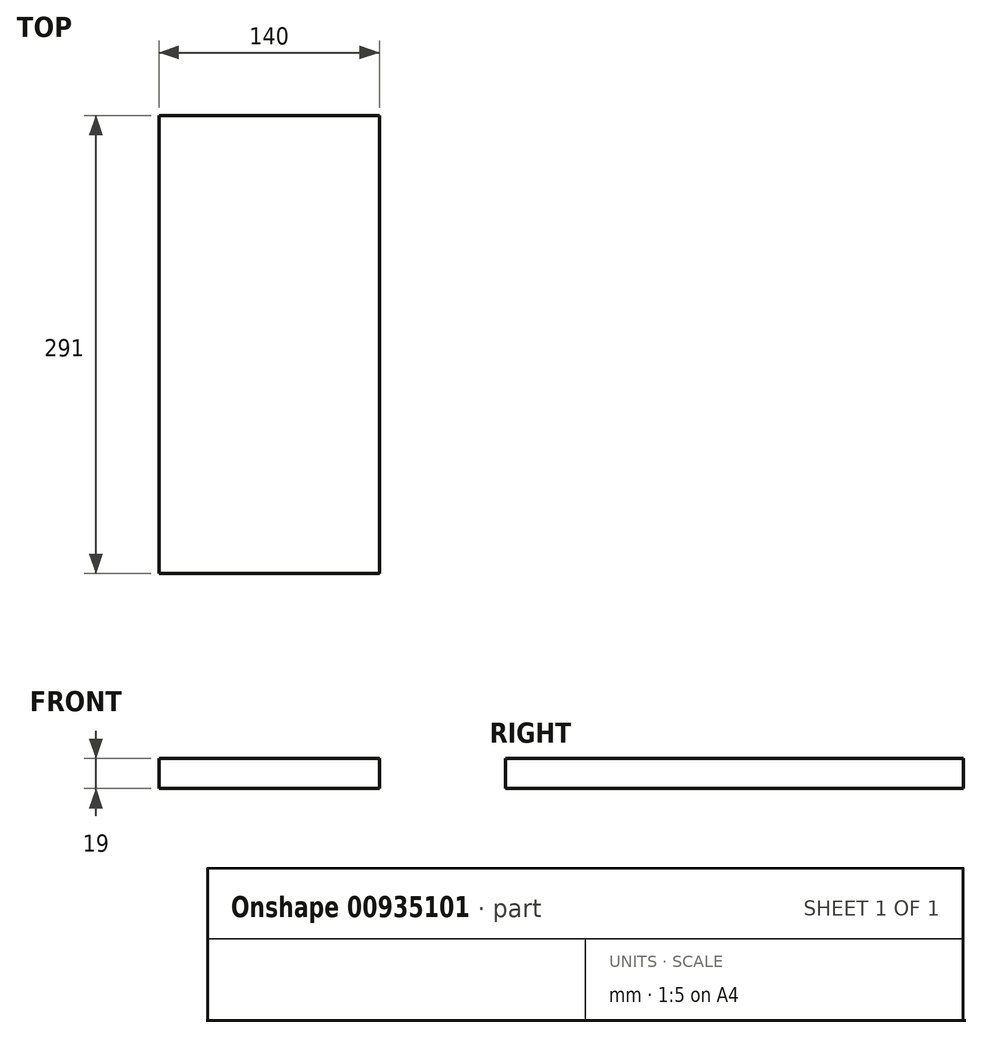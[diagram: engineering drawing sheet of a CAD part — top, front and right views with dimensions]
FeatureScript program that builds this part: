
annotation { "Feature Type Name" : "Feature", "Feature Type Description" : "" }
export const myFeature = defineFeature(function(context is Context, id is Id, definition is map)
    precondition{}
    {
        {
            var Q0;
            Q0=qCreatedBy(makeId("Front.planeOp"),FACE);
            var sketch = newSketch(context, id + "F0", { "sketchPlane" : qUnion([Q0])});
            skLineSegment(sketch, "E0.bottom", {"start": v(0, 0) * mm, "end": v(140, 0) * mm});
            skLineSegment(sketch, "E0.top", {"start": v(0, 19) * mm, "end": v(140, 19) * mm});
            skLineSegment(sketch, "E0.left", {"start": v(0, 0) * mm, "end": v(0, 19) * mm});
            skLineSegment(sketch, "E0.right", {"start": v(140, 0) * mm, "end": v(140, 19) * mm});
            skSolve(sketch);
        }
        {
            var Q0;
            Q0=makeQuery(id+"F0.imprint","IMPRINT",FACE,{"disambiguationData":[TD([[makeQuery(id+"F0.imprint","IMPRINT",EDGE,{"derivedFrom":sQuery(id+"F0.wireOp",EDGE,"E0.bottom")}),1.0]])]});
            extrude(context, id + "F1", {"entities" : qUnion([Q0]), "depth" : 565 * mm - 274 * mm, "offsetDistance" : 25 * mm});
        }
    });
